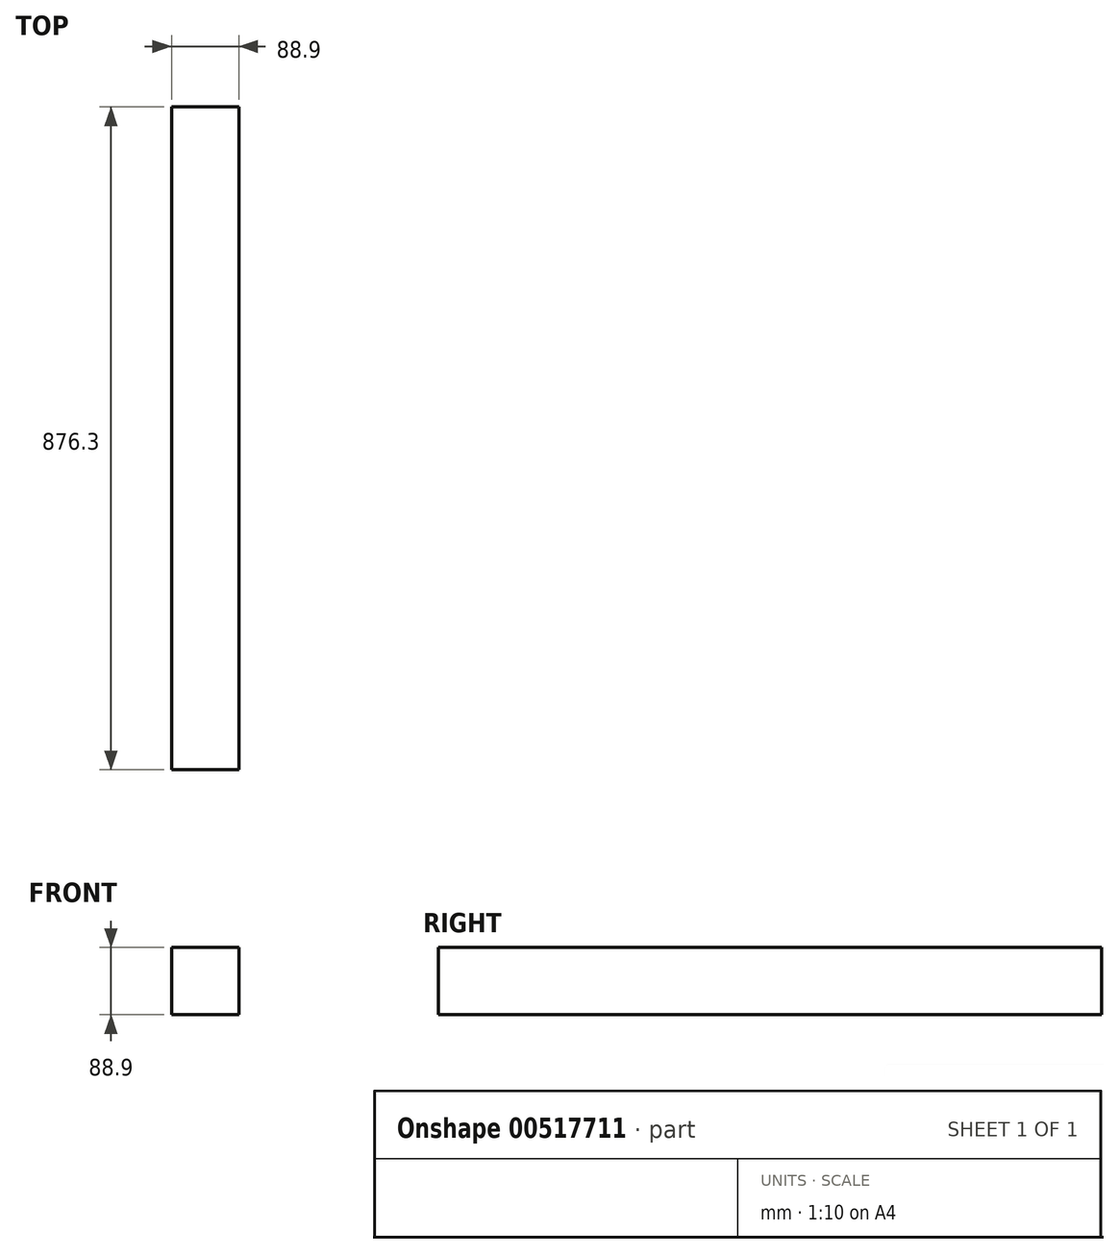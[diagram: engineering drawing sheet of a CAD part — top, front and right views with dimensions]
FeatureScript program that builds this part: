
annotation { "Feature Type Name" : "Feature", "Feature Type Description" : "" }
export const myFeature = defineFeature(function(context is Context, id is Id, definition is map)
    precondition{}
    {
        {
            var Q0;
            Q0=qCreatedBy(makeId("Front.planeOp"),FACE);
            var sketch = newSketch(context, id + "F0", { "sketchPlane" : qUnion([Q0])});
            skLineSegment(sketch, "E0.bottom", {"start": v(44.45, 44.45) * mm, "end": v(-44.45, 44.45) * mm});
            skLineSegment(sketch, "E0.top", {"start": v(44.45, -44.45) * mm, "end": v(-44.45, -44.45) * mm});
            skLineSegment(sketch, "E0.left", {"start": v(44.45, 44.45) * mm, "end": v(44.45, -44.45) * mm});
            skLineSegment(sketch, "E0.right", {"start": v(-44.45, 44.45) * mm, "end": v(-44.45, -44.45) * mm});
            skPoint(sketch, "E0.middle", {"position": v(0, 0) * mm});
            skSolve(sketch);
        }
        {
            var Q0;
            Q0 = qSketchRegion(id + "F0", true);
            var Q1;
            Q1=makeQuery(id+"F0.imprint","IMPRINT",FACE,{"disambiguationData":[TD([[makeQuery(id+"F0.imprint","IMPRINT",EDGE,{"derivedFrom":sQuery(id+"F0.wireOp",EDGE,"E0.bottom")}),1.0]])]});
            extrude(context, id + "F1", {"entities" : qUnion([Q0, Q1]), "depth" : 876.3 * mm, "offsetDistance" : 25.4 * mm});
        }
    });
